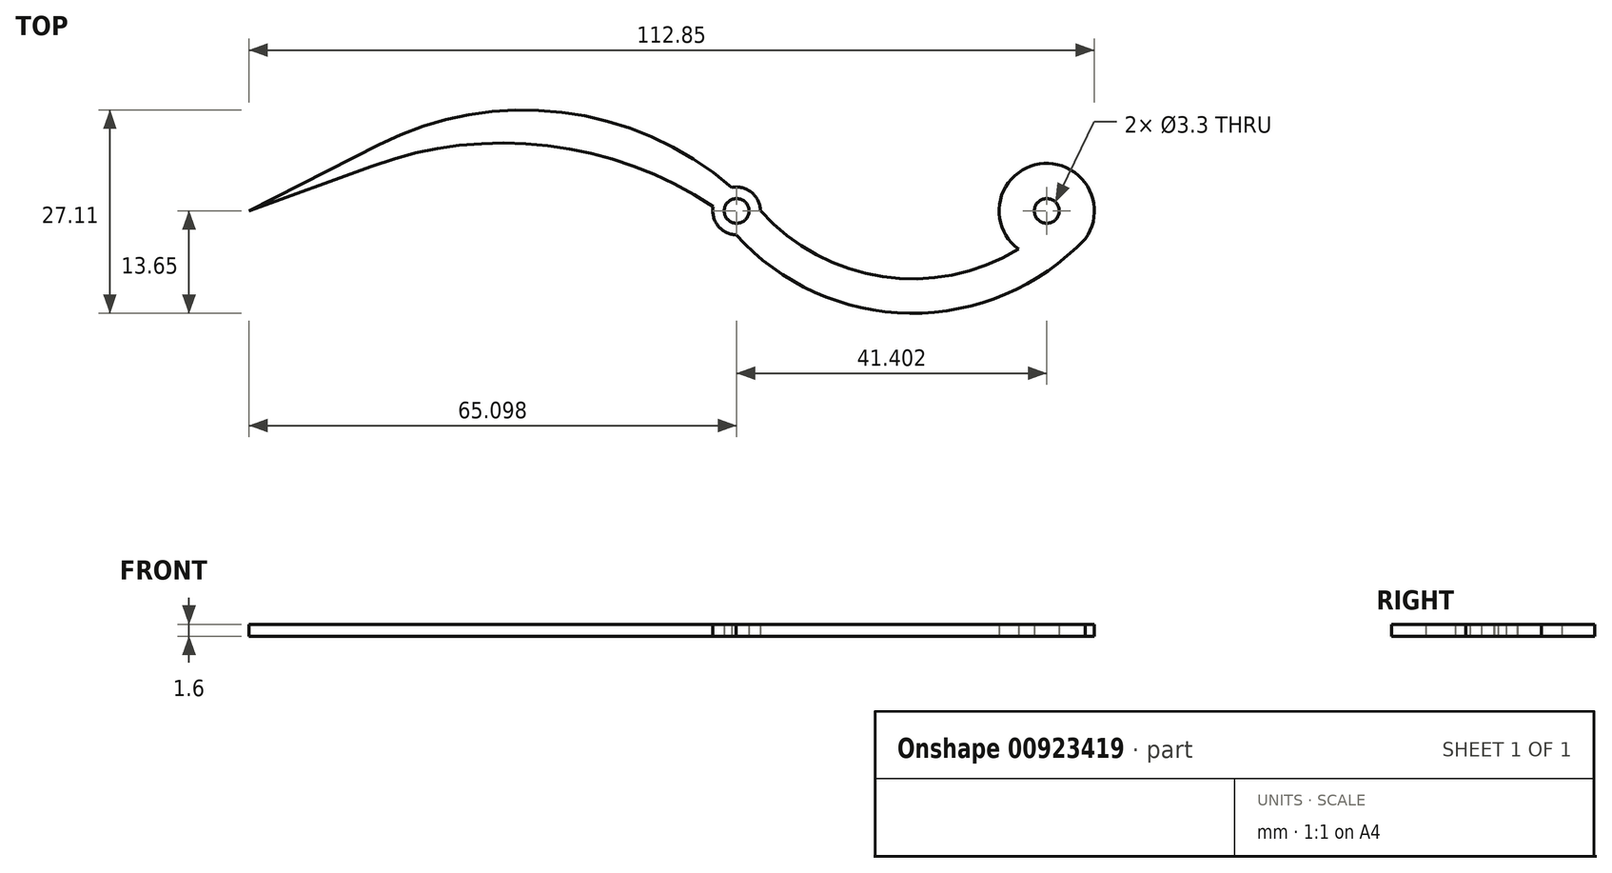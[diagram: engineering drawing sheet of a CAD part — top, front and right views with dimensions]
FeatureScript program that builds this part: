
annotation { "Feature Type Name" : "Feature", "Feature Type Description" : "" }
export const myFeature = defineFeature(function(context is Context, id is Id, definition is map)
    precondition{}
    {
        {
            var Q0;
            Q0=qCreatedBy(makeId("Top.planeOp"),FACE);
            var sketch = newSketch(context, id + "F0", { "sketchPlane" : qUnion([Q0])});
            skArc(sketch, "E0", {"start": v(-38.23, 0.04) * mm, "mid": v(-21.93, -8.78) * mm, "end": v(-3.77, -5.1) * mm});
            skArc(sketch, "E1", {"start": v(-41.48, -3.17) * mm, "mid": v(-18.29, -13.65) * mm, "end": v(5.15, -3.72) * mm});
            skArc(sketch, "E2", {"start": v(5.15, -3.72) * mm, "mid": v(-0.98, 6.27) * mm, "end": v(-3.77, -5.1) * mm});
            skLineSegment(sketch, "E3", {"start": v(-106.5, 0) * mm, "end": v(-89.19, 8.82) * mm});
            skLineSegment(sketch, "E4", {"start": v(-106.5, 0) * mm, "end": v(-90.02, 6) * mm});
            skLineSegment(sketch, "E5", {"start": v(-106.5, 0) * mm, "end": v(-87.48, 0) * mm, "construction": true});
            skArc(sketch, "E6", {"start": v(-44.53, 0.57) * mm, "mid": v(-66.63, 8.7) * mm, "end": v(-90.02, 6) * mm});
            skArc(sketch, "E7", {"start": v(-42.02, 3.11) * mm, "mid": v(-64.73, 13.16) * mm, "end": v(-89.19, 8.82) * mm});
            skArc(sketch, "E8", {"start": v(-38.23, 0.04) * mm, "mid": v(-39.4, 2.47) * mm, "end": v(-42.02, 3.11) * mm});
            skArc(sketch, "E9", {"start": v(-44.53, 0.57) * mm, "mid": v(-43.87, -2) * mm, "end": v(-41.48, -3.17) * mm});
            skLineSegment(sketch, "E10", {"start": v(-69.85, -29.13) * mm, "end": v(-72.64, -41.74) * mm, "construction": true});
            skCircle(sketch, "E11", {"center": v(-41.4, 0) * mm, "radius": 1.65 * mm});
            skCircle(sketch, "E12", {"center": v(0, 0) * mm, "radius": 1.65 * mm});
            skSolve(sketch);
        }
        {
            var Q0;
            Q0=qSketchRegion(id+"F0",true);
            extrude(context, id + "F1", {"entities" : qUnion([Q0]), "depth" : 1.6 * mm, "offsetDistance" : 25.4 * mm});
        }
    });
